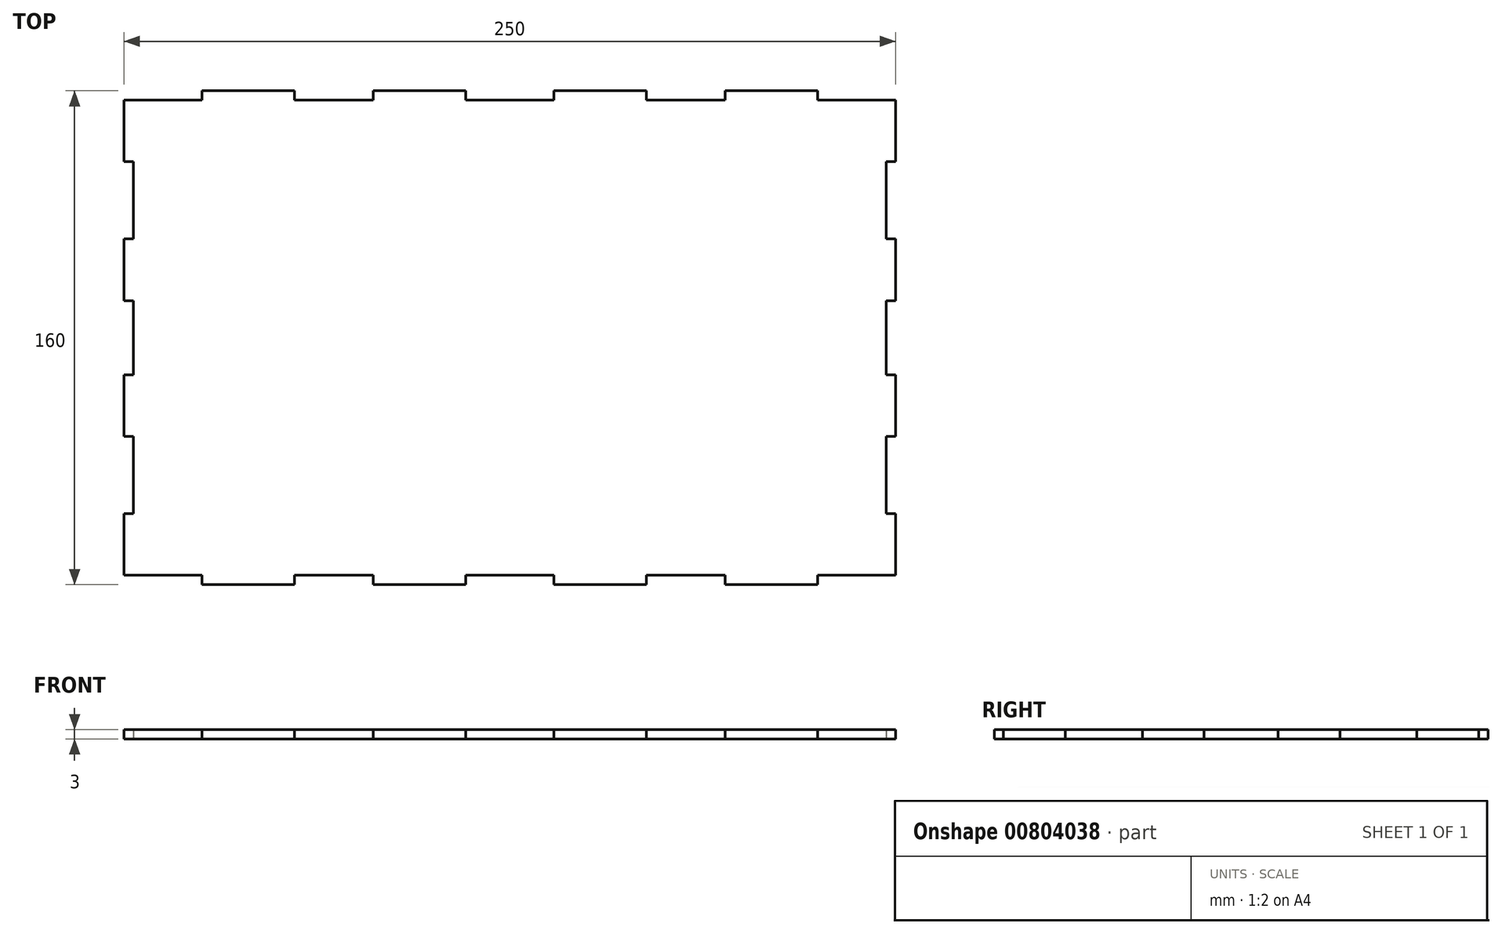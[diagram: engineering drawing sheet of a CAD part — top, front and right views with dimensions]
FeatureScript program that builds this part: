
annotation { "Feature Type Name" : "Feature", "Feature Type Description" : "" }
export const myFeature = defineFeature(function(context is Context, id is Id, definition is map)
    precondition{}
    {
        {
            var Q0;
            Q0=qCreatedBy(makeId("Top.planeOp"),FACE);
            var sketch = newSketch(context, id + "F0", { "sketchPlane" : qUnion([Q0])});
            skPoint(sketch, "E0.middle", {"position": v(0, 0) * mm});
            skLineSegment(sketch, "E1", {"start": v(-84.75, -80) * mm, "end": v(-84.75, -78.5) * mm});
            skLineSegment(sketch, "E2.top", {"start": v(-99.75, -80) * mm, "end": v(-69.75, -80) * mm});
            skLineSegment(sketch, "E2.left", {"start": v(-99.75, -77) * mm, "end": v(-99.75, -80) * mm});
            skLineSegment(sketch, "E2.right", {"start": v(-69.75, -77) * mm, "end": v(-69.75, -80) * mm});
            skPoint(sketch, "E2.middle", {"position": v(-84.75, -78.5) * mm});
            skLineSegment(sketch, "E3", {"start": v(-99.75, -77) * mm, "end": v(-125, -77) * mm});
            skLineSegment(sketch, "E4", {"start": v(-29.25, -80) * mm, "end": v(-29.25, -78.5) * mm});
            skLineSegment(sketch, "E5.top", {"start": v(-44.25, -80) * mm, "end": v(-14.25, -80) * mm});
            skLineSegment(sketch, "E5.left", {"start": v(-44.25, -77) * mm, "end": v(-44.25, -80) * mm});
            skLineSegment(sketch, "E5.right", {"start": v(-14.25, -77) * mm, "end": v(-14.25, -80) * mm});
            skPoint(sketch, "E5.middle", {"position": v(-29.25, -78.5) * mm});
            skLineSegment(sketch, "E6", {"start": v(-69.75, -77) * mm, "end": v(-44.25, -77) * mm});
            skLineSegment(sketch, "E7.MirrorCS", {"start": v(99.75, -77) * mm, "end": v(125, -77) * mm});
            skLineSegment(sketch, "E8.MirrorCS", {"start": v(99.75, -77) * mm, "end": v(99.75, -80) * mm});
            skLineSegment(sketch, "E9.MirrorCS", {"start": v(99.75, -80) * mm, "end": v(69.75, -80) * mm});
            skLineSegment(sketch, "E10.MirrorCS", {"start": v(69.75, -77) * mm, "end": v(69.75, -80) * mm});
            skLineSegment(sketch, "E11.MirrorCS", {"start": v(69.75, -77) * mm, "end": v(44.25, -77) * mm});
            skLineSegment(sketch, "E12.MirrorCS", {"start": v(44.25, -77) * mm, "end": v(44.25, -80) * mm});
            skLineSegment(sketch, "E13.MirrorCS", {"start": v(44.25, -80) * mm, "end": v(14.25, -80) * mm});
            skLineSegment(sketch, "E14.MirrorCS", {"start": v(14.25, -77) * mm, "end": v(14.25, -80) * mm});
            skLineSegment(sketch, "E15", {"start": v(-14.25, -77) * mm, "end": v(14.25, -77) * mm});
            skLineSegment(sketch, "E16.MirrorCS", {"start": v(-99.75, 77) * mm, "end": v(-125, 77) * mm});
            skLineSegment(sketch, "E17.MirrorCS", {"start": v(-99.75, 77) * mm, "end": v(-99.75, 80) * mm});
            skLineSegment(sketch, "E18.MirrorCS", {"start": v(-99.75, 80) * mm, "end": v(-69.75, 80) * mm});
            skLineSegment(sketch, "E19.MirrorCS", {"start": v(-69.75, 77) * mm, "end": v(-69.75, 80) * mm});
            skLineSegment(sketch, "E20.MirrorCS", {"start": v(-69.75, 77) * mm, "end": v(-44.25, 77) * mm});
            skLineSegment(sketch, "E21.MirrorCS", {"start": v(-44.25, 77) * mm, "end": v(-44.25, 80) * mm});
            skLineSegment(sketch, "E22.MirrorCS", {"start": v(-44.25, 80) * mm, "end": v(-14.25, 80) * mm});
            skLineSegment(sketch, "E23.MirrorCS", {"start": v(-14.25, 77) * mm, "end": v(-14.25, 80) * mm});
            skLineSegment(sketch, "E24.MirrorCS", {"start": v(-14.25, 77) * mm, "end": v(14.25, 77) * mm});
            skLineSegment(sketch, "E25.MirrorCS", {"start": v(14.25, 77) * mm, "end": v(14.25, 80) * mm});
            skLineSegment(sketch, "E26.MirrorCS", {"start": v(44.25, 80) * mm, "end": v(14.25, 80) * mm});
            skLineSegment(sketch, "E27.MirrorCS", {"start": v(44.25, 77) * mm, "end": v(44.25, 80) * mm});
            skLineSegment(sketch, "E28.MirrorCS", {"start": v(69.75, 77) * mm, "end": v(44.25, 77) * mm});
            skLineSegment(sketch, "E29.MirrorCS", {"start": v(69.75, 77) * mm, "end": v(69.75, 80) * mm});
            skLineSegment(sketch, "E30.MirrorCS", {"start": v(99.75, 80) * mm, "end": v(69.75, 80) * mm});
            skLineSegment(sketch, "E31.MirrorCS", {"start": v(99.75, 77) * mm, "end": v(99.75, 80) * mm});
            skLineSegment(sketch, "E32", {"start": v(125, 77) * mm, "end": v(125, 57) * mm});
            skLineSegment(sketch, "E33", {"start": v(125, 57) * mm, "end": v(122, 57) * mm});
            skLineSegment(sketch, "E34", {"start": v(122, 57) * mm, "end": v(122, 32) * mm});
            skLineSegment(sketch, "E35", {"start": v(122, 32) * mm, "end": v(125, 32) * mm});
            skLineSegment(sketch, "E36.MirrorCS", {"start": v(125, -77) * mm, "end": v(125, -57) * mm});
            skLineSegment(sketch, "E37.MirrorCS", {"start": v(125, -57) * mm, "end": v(122, -57) * mm});
            skLineSegment(sketch, "E38.MirrorCS", {"start": v(122, -57) * mm, "end": v(122, -32) * mm});
            skLineSegment(sketch, "E39.MirrorCS", {"start": v(122, -32) * mm, "end": v(125, -32) * mm});
            skLineSegment(sketch, "E40", {"start": v(125, 32) * mm, "end": v(125, 12) * mm});
            skLineSegment(sketch, "E41", {"start": v(125, 12) * mm, "end": v(122, 12) * mm});
            skLineSegment(sketch, "E42.MirrorCS", {"start": v(125, -32) * mm, "end": v(125, -12) * mm});
            skLineSegment(sketch, "E43.MirrorCS", {"start": v(125, -12) * mm, "end": v(122, -12) * mm});
            skLineSegment(sketch, "E44", {"start": v(122, 12) * mm, "end": v(122, -12) * mm});
            skLineSegment(sketch, "E45", {"start": v(99.75, 77) * mm, "end": v(125, 77) * mm});
            skLineSegment(sketch, "E46.MirrorCS", {"start": v(-125, 57) * mm, "end": v(-122, 57) * mm});
            skLineSegment(sketch, "E47.MirrorCS", {"start": v(-122, -32) * mm, "end": v(-125, -32) * mm});
            skLineSegment(sketch, "E48.MirrorCS", {"start": v(-122, 32) * mm, "end": v(-125, 32) * mm});
            skLineSegment(sketch, "E49.MirrorCS", {"start": v(-125, -57) * mm, "end": v(-122, -57) * mm});
            skLineSegment(sketch, "E50.MirrorCS", {"start": v(-125, -12) * mm, "end": v(-122, -12) * mm});
            skLineSegment(sketch, "E51.MirrorCS", {"start": v(-125, 12) * mm, "end": v(-122, 12) * mm});
            skLineSegment(sketch, "E52.MirrorCS", {"start": v(-125, -77) * mm, "end": v(-125, -57) * mm});
            skLineSegment(sketch, "E53.MirrorCS", {"start": v(-122, 12) * mm, "end": v(-122, -12) * mm});
            skLineSegment(sketch, "E54.MirrorCS", {"start": v(-122, 57) * mm, "end": v(-122, 32) * mm});
            skLineSegment(sketch, "E55.MirrorCS", {"start": v(-125, 77) * mm, "end": v(-125, 57) * mm});
            skLineSegment(sketch, "E56.MirrorCS", {"start": v(-122, -57) * mm, "end": v(-122, -32) * mm});
            skLineSegment(sketch, "E57.MirrorCS", {"start": v(-125, 32) * mm, "end": v(-125, 12) * mm});
            skLineSegment(sketch, "E58.MirrorCS", {"start": v(-125, -32) * mm, "end": v(-125, -12) * mm});
            skLineSegment(sketch, "E59", {"start": v(123.5, 44.5) * mm, "end": v(125.45, 44.5) * mm});
            skLineSegment(sketch, "E60", {"start": v(122, 32) * mm, "end": v(125, 12) * mm});
            skLineSegment(sketch, "E61", {"start": v(125, 32) * mm, "end": v(122, 12) * mm});
            skLineSegment(sketch, "E62", {"start": v(123.5, 22) * mm, "end": v(125, 22) * mm});
            skSolve(sketch);
        }
        {
            var Q0;
            Q0 = qSketchRegion(id + "F0", true);
            extrude(context, id + "F1", {"entities" : qUnion([Q0]), "depth" : 3 * mm, "offsetDistance" : 25 * mm});
        }
    });
